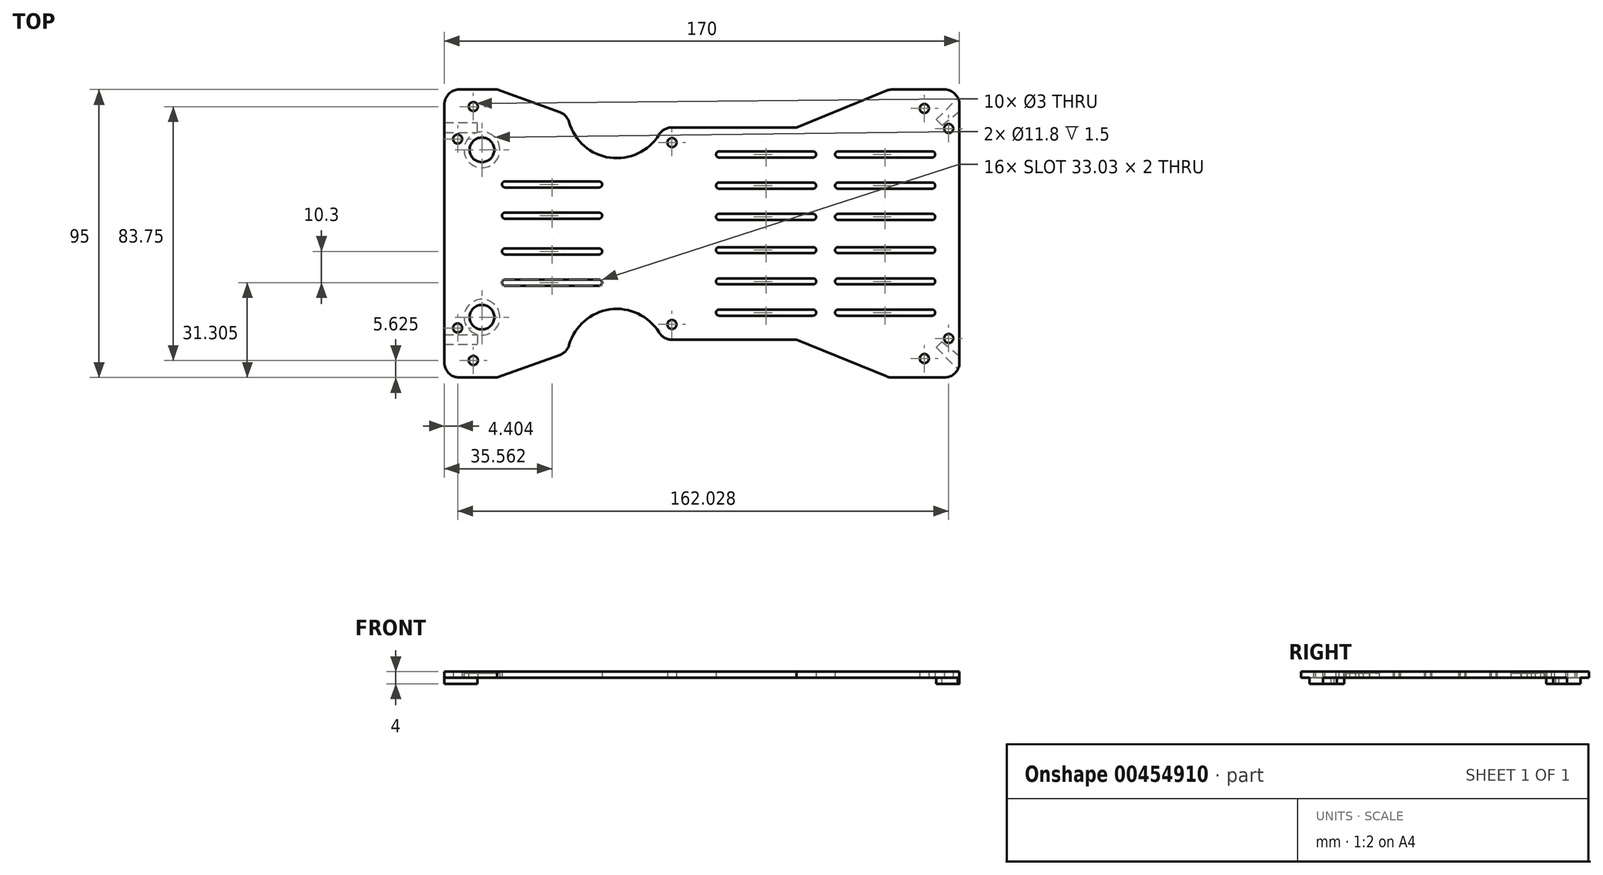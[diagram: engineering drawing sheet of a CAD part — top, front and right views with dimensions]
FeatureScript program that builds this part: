
annotation { "Feature Type Name" : "Feature", "Feature Type Description" : "" }
export const myFeature = defineFeature(function(context is Context, id is Id, definition is map)
    precondition{}
    {
        {
            var Q0;
            Q0=qCreatedBy(makeId("Top.planeOp"),FACE);
            var sketch = newSketch(context, id + "F0", { "sketchPlane" : qUnion([Q0])});
            skLineSegment(sketch, "E0.top", {"start": v(-5, 47.5) * mm, "end": v(-22.22, 47.5) * mm});
            skLineSegment(sketch, "E0.left", {"start": v(0, 35) * mm, "end": v(0, 42.5) * mm});
            skPoint(sketch, "E1.startSnap0", {"position": v(-23.2, 41.25) * mm});
            skPoint(sketch, "E1.startSnap1", {"position": v(-11.6, 47.5) * mm});
            skArc(sketch, "E2", {"start": v(-128.81, 36.72) * mm, "mid": v(-115.3, 25.02) * mm, "end": v(-99.14, 32.63) * mm});
            skLineSegment(sketch, "E3.trimOffspring", {"start": v(-94.88, 35) * mm, "end": v(-53.78, 35) * mm});
            skPoint(sketch, "E1.start.orphan", {"position": v(-11.6, 41.25) * mm});
            skCircle(sketch, "E4", {"center": v(-113.07, 41.25) * mm, "radius": 12.55 * mm, "construction": true});
            skLineSegment(sketch, "E5.top", {"start": v(-165, 47.5) * mm, "end": v(-149.65, 47.5) * mm});
            skLineSegment(sketch, "E5.left", {"start": v(-170, 35) * mm, "end": v(-170, 42.5) * mm});
            skLineSegment(sketch, "E6", {"start": v(-160.43, 41.87) * mm, "end": v(-136.46, 59) * mm, "construction": true});
            skPoint(sketch, "E6.startSnap0", {"position": v(-149.65, 47.5) * mm});
            skPoint(sketch, "E6.startSnap1", {"position": v(-170, 41.25) * mm});
            skLineSegment(sketch, "E7", {"start": v(-136.46, 59) * mm, "end": v(-62.44, 61.85) * mm, "construction": true});
            skLineSegment(sketch, "E8", {"start": v(-160.43, 41.87) * mm, "end": v(-62.44, 61.85) * mm, "construction": true});
            skCircle(sketch, "E9", {"center": v(-62.44, 61.85) * mm, "radius": 12.62 * mm, "construction": true});
            skLineSegment(sketch, "E10", {"start": v(-24.11, 47.13) * mm, "end": v(-53.78, 35) * mm});
            skCircle(sketch, "E11", {"center": v(-157.56, 27.6) * mm, "radius": 4.06 * mm});
            skPoint(sketch, "E0.bottom.end.orphan", {"position": v(-23.2, 35) * mm});
            skPoint(sketch, "E12.middle", {"position": v(-37.46, 31.5) * mm});
            skLineSegment(sketch, "E13", {"start": v(-131.92, 40.04) * mm, "end": v(-152.56, 47.5) * mm});
            skPoint(sketch, "E5.right.end.orphan", {"position": v(-129.3, 47.5) * mm});
            skPoint(sketch, "E14.visualSharp", {"position": v(-170, 47.5) * mm});
            skArc(sketch, "E14.filletArc", {"start": v(-165, 47.5) * mm, "mid": v(-168.54, 46.04) * mm, "end": v(-170, 42.5) * mm});
            skLineSegment(sketch, "E15", {"start": v(-2.46, 0) * mm, "end": v(-170, 0) * mm, "construction": true});
            skLineSegment(sketch, "E16", {"start": v(0, 35) * mm, "end": v(0, 0) * mm});
            skLineSegment(sketch, "E17", {"start": v(-170, 35) * mm, "end": v(-170, 0) * mm});
            skPoint(sketch, "E18.visualSharp", {"position": v(-129.3, 39.1) * mm});
            skArc(sketch, "E18.filletArc", {"start": v(-128.81, 36.72) * mm, "mid": v(-129.96, 38.75) * mm, "end": v(-131.92, 40.04) * mm});
            skPoint(sketch, "E19.visualSharp", {"position": v(-23.2, 47.5) * mm});
            skArc(sketch, "E19.filletArc", {"start": v(-22.22, 47.5) * mm, "mid": v(-23.19, 47.4) * mm, "end": v(-24.11, 47.13) * mm});
            skPoint(sketch, "E20.visualSharp", {"position": v(0, 47.5) * mm});
            skArc(sketch, "E20.filletArc", {"start": v(0, 42.5) * mm, "mid": v(-1.46, 46.04) * mm, "end": v(-5, 47.5) * mm});
            skPoint(sketch, "E21.visualSharp", {"position": v(-97.92, 35) * mm});
            skArc(sketch, "E21.filletArc", {"start": v(-94.88, 35) * mm, "mid": v(-97.32, 34.37) * mm, "end": v(-99.14, 32.63) * mm});
            skCircle(sketch, "E22", {"center": v(-94.88, 30) * mm, "radius": 1.5 * mm});
            skCircle(sketch, "E23", {"center": v(-165.6, 31.16) * mm, "radius": 1.5 * mm});
            skCircle(sketch, "E24", {"center": v(-3.57, 34.62) * mm, "radius": 1.5 * mm});
            skCircle(sketch, "E25", {"center": v(-11.6, 41.25) * mm, "radius": 1.5 * mm});
            skCircle(sketch, "E26", {"center": v(-160.43, 41.87) * mm, "radius": 1.5 * mm});
            skLineSegment(sketch, "E27", {"start": v(-9, 26.08) * mm, "end": v(-40.04, 26.08) * mm, "construction": true});
            skArc(sketch, "E28.0.startCap", {"start": v(-9, 27.08) * mm, "mid": v(-8, 26.08) * mm, "end": v(-9, 25.08) * mm});
            skArc(sketch, "E28.0.endCap", {"start": v(-40.04, 25.08) * mm, "mid": v(-41.04, 26.08) * mm, "end": v(-40.04, 27.08) * mm});
            skLineSegment(sketch, "E28.0.left", {"start": v(-9, 25.08) * mm, "end": v(-40.04, 25.08) * mm});
            skLineSegment(sketch, "E28.0.right", {"start": v(-9, 27.08) * mm, "end": v(-40.04, 27.08) * mm});
            skLineSegment(sketch, "E29.0.1.0", {"start": v(-9, 16.78) * mm, "end": v(-40.04, 16.78) * mm});
            skLineSegment(sketch, "E29.0.1.1", {"start": v(-9, 14.78) * mm, "end": v(-40.04, 14.78) * mm});
            skLineSegment(sketch, "E29.0.1.2", {"start": v(-9, 15.78) * mm, "end": v(-40.04, 15.78) * mm, "construction": true});
            skArc(sketch, "E29.0.1.3", {"start": v(-9, 16.78) * mm, "mid": v(-8, 15.78) * mm, "end": v(-9, 14.78) * mm});
            skArc(sketch, "E29.0.1.4", {"start": v(-40.04, 14.78) * mm, "mid": v(-41.04, 15.78) * mm, "end": v(-40.04, 16.78) * mm});
            skLineSegment(sketch, "E29.0.2.0", {"start": v(-9, 6.48) * mm, "end": v(-40.04, 6.48) * mm});
            skLineSegment(sketch, "E29.0.2.1", {"start": v(-9, 4.48) * mm, "end": v(-40.04, 4.48) * mm});
            skLineSegment(sketch, "E29.0.2.2", {"start": v(-9, 5.48) * mm, "end": v(-40.04, 5.48) * mm, "construction": true});
            skArc(sketch, "E29.0.2.3", {"start": v(-9, 6.48) * mm, "mid": v(-8, 5.48) * mm, "end": v(-9, 4.48) * mm});
            skArc(sketch, "E29.0.2.4", {"start": v(-40.04, 4.48) * mm, "mid": v(-41.04, 5.48) * mm, "end": v(-40.04, 6.48) * mm});
            skLineSegment(sketch, "E29.1.0.0", {"start": v(-48.3, 27.08) * mm, "end": v(-79.34, 27.08) * mm});
            skLineSegment(sketch, "E29.1.0.1", {"start": v(-48.3, 25.08) * mm, "end": v(-79.34, 25.08) * mm});
            skLineSegment(sketch, "E29.1.0.2", {"start": v(-48.3, 26.08) * mm, "end": v(-79.34, 26.08) * mm, "construction": true});
            skArc(sketch, "E29.1.0.3", {"start": v(-48.3, 27.08) * mm, "mid": v(-47.3, 26.08) * mm, "end": v(-48.3, 25.08) * mm});
            skArc(sketch, "E29.1.0.4", {"start": v(-79.34, 25.08) * mm, "mid": v(-80.34, 26.08) * mm, "end": v(-79.34, 27.08) * mm});
            skLineSegment(sketch, "E29.1.1.0", {"start": v(-48.3, 16.78) * mm, "end": v(-79.34, 16.78) * mm});
            skLineSegment(sketch, "E29.1.1.1", {"start": v(-48.3, 14.78) * mm, "end": v(-79.34, 14.78) * mm});
            skLineSegment(sketch, "E29.1.1.2", {"start": v(-48.3, 15.78) * mm, "end": v(-79.34, 15.78) * mm, "construction": true});
            skArc(sketch, "E29.1.1.3", {"start": v(-48.3, 16.78) * mm, "mid": v(-47.3, 15.78) * mm, "end": v(-48.3, 14.78) * mm});
            skArc(sketch, "E29.1.1.4", {"start": v(-79.34, 14.78) * mm, "mid": v(-80.34, 15.78) * mm, "end": v(-79.34, 16.78) * mm});
            skLineSegment(sketch, "E29.1.2.0", {"start": v(-48.3, 6.48) * mm, "end": v(-79.34, 6.48) * mm});
            skLineSegment(sketch, "E29.1.2.1", {"start": v(-48.3, 4.48) * mm, "end": v(-79.34, 4.48) * mm});
            skLineSegment(sketch, "E29.1.2.2", {"start": v(-48.3, 5.48) * mm, "end": v(-79.34, 5.48) * mm, "construction": true});
            skArc(sketch, "E29.1.2.3", {"start": v(-48.3, 6.48) * mm, "mid": v(-47.3, 5.48) * mm, "end": v(-48.3, 4.48) * mm});
            skArc(sketch, "E29.1.2.4", {"start": v(-79.34, 4.48) * mm, "mid": v(-80.34, 5.48) * mm, "end": v(-79.34, 6.48) * mm});
            skLineSegment(sketch, "E29.direction1", {"start": v(-40.04, 25.08) * mm, "end": v(-79.34, 25.08) * mm, "construction": true});
            skLineSegment(sketch, "E29.direction2", {"start": v(-40.04, 25.08) * mm, "end": v(-40.04, 14.78) * mm, "construction": true});
            skLineSegment(sketch, "E30.1.1.0", {"start": v(-118.92, 17.2) * mm, "end": v(-149.95, 17.2) * mm});
            skLineSegment(sketch, "E30.1.1.1", {"start": v(-118.92, 15.2) * mm, "end": v(-149.95, 15.2) * mm});
            skLineSegment(sketch, "E30.1.1.2", {"start": v(-118.92, 16.2) * mm, "end": v(-149.95, 16.2) * mm, "construction": true});
            skArc(sketch, "E30.1.1.3", {"start": v(-118.92, 17.2) * mm, "mid": v(-117.92, 16.2) * mm, "end": v(-118.92, 15.2) * mm});
            skArc(sketch, "E30.1.1.4", {"start": v(-149.95, 15.2) * mm, "mid": v(-150.95, 16.2) * mm, "end": v(-149.95, 17.2) * mm});
            skLineSegment(sketch, "E30.1.2.0", {"start": v(-118.92, 6.9) * mm, "end": v(-149.95, 6.9) * mm});
            skLineSegment(sketch, "E30.1.2.1", {"start": v(-118.92, 4.9) * mm, "end": v(-149.95, 4.9) * mm});
            skLineSegment(sketch, "E30.1.2.2", {"start": v(-118.92, 5.9) * mm, "end": v(-149.95, 5.9) * mm, "construction": true});
            skArc(sketch, "E30.1.2.3", {"start": v(-118.92, 6.9) * mm, "mid": v(-117.92, 5.9) * mm, "end": v(-118.92, 4.9) * mm});
            skArc(sketch, "E30.1.2.4", {"start": v(-149.95, 4.9) * mm, "mid": v(-150.95, 5.9) * mm, "end": v(-149.95, 6.9) * mm});
            skLineSegment(sketch, "E31.MirrorCS", {"start": v(-40.04, -25.08) * mm, "end": v(-40.04, -14.78) * mm, "construction": true});
            skLineSegment(sketch, "E32.MirrorCS", {"start": v(-170, -35) * mm, "end": v(-170, -42.5) * mm});
            skLineSegment(sketch, "E33.MirrorCS", {"start": v(0, -35) * mm, "end": v(0, -42.5) * mm});
            skLineSegment(sketch, "E34.MirrorCS", {"start": v(-48.3, -6.48) * mm, "end": v(-79.34, -6.48) * mm});
            skLineSegment(sketch, "E35.MirrorCS", {"start": v(-9, -6.48) * mm, "end": v(-40.04, -6.48) * mm});
            skLineSegment(sketch, "E36.MirrorCS", {"start": v(-118.92, -15.2) * mm, "end": v(-149.95, -15.2) * mm});
            skLineSegment(sketch, "E37.MirrorCS", {"start": v(-5, -47.5) * mm, "end": v(-22.22, -47.5) * mm});
            skLineSegment(sketch, "E38.MirrorCS", {"start": v(-9, -14.78) * mm, "end": v(-40.04, -14.78) * mm});
            skLineSegment(sketch, "E39.MirrorCS", {"start": v(-48.3, -14.78) * mm, "end": v(-79.34, -14.78) * mm});
            skCircle(sketch, "E40.MirrorC", {"center": v(-157.56, -27.6) * mm, "radius": 4.06 * mm});
            skLineSegment(sketch, "E41.MirrorCS", {"start": v(-118.92, -6.9) * mm, "end": v(-149.95, -6.9) * mm});
            skLineSegment(sketch, "E42.MirrorCS", {"start": v(-165, -47.5) * mm, "end": v(-149.65, -47.5) * mm});
            skPoint(sketch, "E43.MirrorP", {"position": v(-37.46, -31.5) * mm});
            skLineSegment(sketch, "E44.MirrorCS", {"start": v(-118.92, -5.9) * mm, "end": v(-149.95, -5.9) * mm, "construction": true});
            skPoint(sketch, "E45.MirrorP", {"position": v(-129.3, -47.5) * mm});
            skLineSegment(sketch, "E46.MirrorCS", {"start": v(-9, -15.78) * mm, "end": v(-40.04, -15.78) * mm, "construction": true});
            skPoint(sketch, "E47.MirrorP", {"position": v(-23.2, -35) * mm});
            skLineSegment(sketch, "E48.MirrorCS", {"start": v(-48.3, -4.48) * mm, "end": v(-79.34, -4.48) * mm});
            skPoint(sketch, "E49.MirrorP", {"position": v(-170, -47.5) * mm});
            skLineSegment(sketch, "E50.MirrorCS", {"start": v(-48.3, -5.48) * mm, "end": v(-79.34, -5.48) * mm, "construction": true});
            skLineSegment(sketch, "E51.MirrorCS", {"start": v(-9, -4.48) * mm, "end": v(-40.04, -4.48) * mm});
            skLineSegment(sketch, "E52.MirrorCS", {"start": v(-9, -5.48) * mm, "end": v(-40.04, -5.48) * mm, "construction": true});
            skPoint(sketch, "E53.MirrorP", {"position": v(-129.3, -39.1) * mm});
            skLineSegment(sketch, "E54.MirrorCS", {"start": v(-40.04, -25.08) * mm, "end": v(-79.34, -25.08) * mm, "construction": true});
            skPoint(sketch, "E55.MirrorP", {"position": v(-23.2, -41.25) * mm});
            skPoint(sketch, "E56.MirrorP", {"position": v(-11.6, -41.25) * mm});
            skPoint(sketch, "E57.MirrorP", {"position": v(0, -47.5) * mm});
            skLineSegment(sketch, "E58.MirrorCS", {"start": v(-48.3, -27.08) * mm, "end": v(-79.34, -27.08) * mm});
            skPoint(sketch, "E59.MirrorP", {"position": v(-23.2, -47.5) * mm});
            skLineSegment(sketch, "E60.MirrorCS", {"start": v(-160.43, -41.87) * mm, "end": v(-62.44, -61.85) * mm, "construction": true});
            skCircle(sketch, "E61.MirrorC", {"center": v(-113.07, -41.25) * mm, "radius": 12.55 * mm, "construction": true});
            skLineSegment(sketch, "E62.MirrorCS", {"start": v(-24.11, -47.13) * mm, "end": v(-53.78, -35) * mm});
            skLineSegment(sketch, "E63.MirrorCS", {"start": v(-94.88, -35) * mm, "end": v(-53.78, -35) * mm});
            skLineSegment(sketch, "E64.MirrorCS", {"start": v(-9, -25.08) * mm, "end": v(-40.04, -25.08) * mm});
            skLineSegment(sketch, "E65.MirrorCS", {"start": v(-160.43, -41.87) * mm, "end": v(-136.46, -59) * mm, "construction": true});
            skLineSegment(sketch, "E66.MirrorCS", {"start": v(-9, -16.78) * mm, "end": v(-40.04, -16.78) * mm});
            skLineSegment(sketch, "E67.MirrorCS", {"start": v(-48.3, -26.08) * mm, "end": v(-79.34, -26.08) * mm, "construction": true});
            skLineSegment(sketch, "E68.MirrorCS", {"start": v(-136.46, -59) * mm, "end": v(-62.44, -61.85) * mm, "construction": true});
            skPoint(sketch, "E69.MirrorP", {"position": v(-170, -41.25) * mm});
            skLineSegment(sketch, "E70.MirrorCS", {"start": v(-9, -26.08) * mm, "end": v(-40.04, -26.08) * mm, "construction": true});
            skLineSegment(sketch, "E71.MirrorCS", {"start": v(-118.92, -17.2) * mm, "end": v(-149.95, -17.2) * mm});
            skLineSegment(sketch, "E72.MirrorCS", {"start": v(0, -35) * mm, "end": v(0, 0) * mm});
            skPoint(sketch, "E73.MirrorP", {"position": v(-97.92, -35) * mm});
            skCircle(sketch, "E74.MirrorC", {"center": v(-62.44, -61.85) * mm, "radius": 12.62 * mm, "construction": true});
            skPoint(sketch, "E75.MirrorP", {"position": v(-11.6, -47.5) * mm});
            skArc(sketch, "E76.MirrorCS", {"start": v(-128.81, -36.72) * mm, "mid": v(-115.3, -25.02) * mm, "end": v(-99.14, -32.63) * mm});
            skLineSegment(sketch, "E77.MirrorCS", {"start": v(-9, -27.08) * mm, "end": v(-40.04, -27.08) * mm});
            skLineSegment(sketch, "E78.MirrorCS", {"start": v(-48.3, -16.78) * mm, "end": v(-79.34, -16.78) * mm});
            skLineSegment(sketch, "E79.MirrorCS", {"start": v(-118.92, -16.2) * mm, "end": v(-149.95, -16.2) * mm, "construction": true});
            skLineSegment(sketch, "E80.MirrorCS", {"start": v(-48.3, -15.78) * mm, "end": v(-79.34, -15.78) * mm, "construction": true});
            skLineSegment(sketch, "E81.MirrorCS", {"start": v(-118.92, -4.9) * mm, "end": v(-149.95, -4.9) * mm});
            skPoint(sketch, "E82.MirrorP", {"position": v(-149.65, -47.5) * mm});
            skLineSegment(sketch, "E83.MirrorCS", {"start": v(-170, -35) * mm, "end": v(-170, 0) * mm});
            skLineSegment(sketch, "E84.MirrorCS", {"start": v(-131.92, -40.04) * mm, "end": v(-152.56, -47.5) * mm});
            skArc(sketch, "E85.MirrorCS", {"start": v(-118.92, -6.9) * mm, "mid": v(-117.92, -5.9) * mm, "end": v(-118.92, -4.9) * mm});
            skArc(sketch, "E86.MirrorCS", {"start": v(-9, -27.08) * mm, "mid": v(-8, -26.08) * mm, "end": v(-9, -25.08) * mm});
            skArc(sketch, "E87.MirrorCS", {"start": v(-40.04, -25.08) * mm, "mid": v(-41.04, -26.08) * mm, "end": v(-40.04, -27.08) * mm});
            skArc(sketch, "E88.MirrorCS", {"start": v(-149.95, -4.9) * mm, "mid": v(-150.95, -5.9) * mm, "end": v(-149.95, -6.9) * mm});
            skArc(sketch, "E89.MirrorCS", {"start": v(-40.04, -14.78) * mm, "mid": v(-41.04, -15.78) * mm, "end": v(-40.04, -16.78) * mm});
            skCircle(sketch, "E90.MirrorC", {"center": v(-94.88, -30) * mm, "radius": 1.5 * mm});
            skArc(sketch, "E91.MirrorCS", {"start": v(-9, -6.48) * mm, "mid": v(-8, -5.48) * mm, "end": v(-9, -4.48) * mm});
            skArc(sketch, "E92.MirrorCS", {"start": v(-22.22, -47.5) * mm, "mid": v(-23.19, -47.4) * mm, "end": v(-24.11, -47.13) * mm});
            skArc(sketch, "E93.MirrorCS", {"start": v(-79.34, -14.78) * mm, "mid": v(-80.34, -15.78) * mm, "end": v(-79.34, -16.78) * mm});
            skArc(sketch, "E94.MirrorCS", {"start": v(-9, -16.78) * mm, "mid": v(-8, -15.78) * mm, "end": v(-9, -14.78) * mm});
            skCircle(sketch, "E95.MirrorC", {"center": v(-160.43, -41.87) * mm, "radius": 1.5 * mm});
            skArc(sketch, "E96.MirrorCS", {"start": v(-149.95, -15.2) * mm, "mid": v(-150.95, -16.2) * mm, "end": v(-149.95, -17.2) * mm});
            skArc(sketch, "E97.MirrorCS", {"start": v(-128.81, -36.72) * mm, "mid": v(-129.96, -38.75) * mm, "end": v(-131.92, -40.04) * mm});
            skArc(sketch, "E98.MirrorCS", {"start": v(-48.3, -16.78) * mm, "mid": v(-47.3, -15.78) * mm, "end": v(-48.3, -14.78) * mm});
            skArc(sketch, "E99.MirrorCS", {"start": v(-94.88, -35) * mm, "mid": v(-97.32, -34.37) * mm, "end": v(-99.14, -32.63) * mm});
            skArc(sketch, "E100.MirrorCS", {"start": v(-48.3, -6.48) * mm, "mid": v(-47.3, -5.48) * mm, "end": v(-48.3, -4.48) * mm});
            skArc(sketch, "E101.MirrorCS", {"start": v(-79.34, -4.48) * mm, "mid": v(-80.34, -5.48) * mm, "end": v(-79.34, -6.48) * mm});
            skArc(sketch, "E102.MirrorCS", {"start": v(-40.04, -4.48) * mm, "mid": v(-41.04, -5.48) * mm, "end": v(-40.04, -6.48) * mm});
            skCircle(sketch, "E103.MirrorC", {"center": v(-11.6, -41.25) * mm, "radius": 1.5 * mm});
            skArc(sketch, "E104.MirrorCS", {"start": v(-79.34, -25.08) * mm, "mid": v(-80.34, -26.08) * mm, "end": v(-79.34, -27.08) * mm});
            skArc(sketch, "E105.MirrorCS", {"start": v(-48.3, -27.08) * mm, "mid": v(-47.3, -26.08) * mm, "end": v(-48.3, -25.08) * mm});
            skArc(sketch, "E106.MirrorCS", {"start": v(-118.92, -17.2) * mm, "mid": v(-117.92, -16.2) * mm, "end": v(-118.92, -15.2) * mm});
            skArc(sketch, "E107.MirrorCS", {"start": v(0, -42.5) * mm, "mid": v(-1.46, -46.04) * mm, "end": v(-5, -47.5) * mm});
            skCircle(sketch, "E108.MirrorC", {"center": v(-165.6, -31.16) * mm, "radius": 1.5 * mm});
            skCircle(sketch, "E109.MirrorC", {"center": v(-3.57, -34.62) * mm, "radius": 1.5 * mm});
            skLineSegment(sketch, "E110.MirrorCS", {"start": v(-48.3, -25.08) * mm, "end": v(-79.34, -25.08) * mm});
            skArc(sketch, "E111.MirrorCS", {"start": v(-165, -47.5) * mm, "mid": v(-168.54, -46.04) * mm, "end": v(-170, -42.5) * mm});
            skSolve(sketch);
        }
        {
            var Q0;
            Q0=qSketchRegion(id+"F0",true);
            extrude(context, id + "F1", {"entities" : qUnion([Q0]), "depth" : 2 * mm});
        }
        {
            var Q0;
            Q0=makeQuery(id+"F1.opExtrude","CAP_FACE",FACE,{"disambiguationData":[OSD([sQuery(id+"F0.wireOp",EDGE,"E0.top"),sQuery(id+"F0.wireOp",EDGE,"E0.left"),sQuery(id+"F0.wireOp",EDGE,"E2"),sQuery(id+"F0.wireOp",EDGE,"E3.trimOffspring"),sQuery(id+"F0.wireOp",EDGE,"E5.top"),sQuery(id+"F0.wireOp",EDGE,"E5.left"),sQuery(id+"F0.wireOp",EDGE,"7hJqdO40-9QEB-ep9W-JTcp-znnLO8iOH2ny"),sQuery(id+"F0.wireOp",EDGE,"yaqOU6vn-vtul-Jn4A-1Bdt-kECmfQPkav5v"),sQuery(id+"F0.wireOp",EDGE,"r8IJrCJv-crzM-KIvY-DkAr-MW3v6tCYtiw1"),sQuery(id+"F0.wireOp",EDGE,"jzMd41p7-Ak69-SiEM-pOr1-xVNg9LxxrAfh"),sQuery(id+"F0.wireOp",EDGE,"fxCpGdvF-k1nJ-6rw2-18lv-cCig44xFyPOT"),sQuery(id+"F0.wireOp",EDGE,"3vhJkwcW-7L6n-dbvg-KpTP-31G8Jv8qNSP8"),sQuery(id+"F0.wireOp",EDGE,"9XNVBvv0-zH1r-9cPB-NFeU-YQdWjPXlst3P"),sQuery(id+"F0.wireOp",EDGE,"y3D83JcK-dgKw-NrD8-Es56-h46w4wRxeLdj"),sQuery(id+"F0.wireOp",EDGE,"E10"),sQuery(id+"F0.wireOp",EDGE,"E11"),sQuery(id+"F0.wireOp",EDGE,"axs33Ezf-adaq-kjD9-MvXq-XhUTkXVeFDVn"),sQuery(id+"F0.wireOp",EDGE,"E12.bottom"),sQuery(id+"F0.wireOp",EDGE,"E12.top"),sQuery(id+"F0.wireOp",EDGE,"E12.left"),sQuery(id+"F0.wireOp",EDGE,"E12.right"),sQuery(id+"F0.wireOp",EDGE,"E13"),sQuery(id+"F0.wireOp",EDGE,"E14.filletArc"),sQuery(id+"F0.wireOp",EDGE,"E16"),sQuery(id+"F0.wireOp",EDGE,"E17"),sQuery(id+"F0.wireOp",EDGE,"E18.filletArc"),sQuery(id+"F0.wireOp",EDGE,"E19.filletArc"),sQuery(id+"F0.wireOp",EDGE,"E20.filletArc"),sQuery(id+"F0.wireOp",EDGE,"E21.filletArc"),sQuery(id+"F0.wireOp",EDGE,"E22"),sQuery(id+"F0.wireOp",EDGE,"E23"),sQuery(id+"F0.wireOp",EDGE,"E24"),sQuery(id+"F0.wireOp",EDGE,"dc92d004-a6ad-41b4-b321-0510745f16cf0.MirrorC"),sQuery(id+"F0.wireOp",EDGE,"dc92d004-a6ad-41b4-b321-0510745f16cf1.MirrorCS"),sQuery(id+"F0.wireOp",EDGE,"dc92d004-a6ad-41b4-b321-0510745f16cf2.MirrorC"),sQuery(id+"F0.wireOp",EDGE,"dc92d004-a6ad-41b4-b321-0510745f16cf3.MirrorCS"),sQuery(id+"F0.wireOp",EDGE,"dc92d004-a6ad-41b4-b321-0510745f16cf4.MirrorCS"),sQuery(id+"F0.wireOp",EDGE,"dc92d004-a6ad-41b4-b321-0510745f16cf5.MirrorCS"),sQuery(id+"F0.wireOp",EDGE,"dc92d004-a6ad-41b4-b321-0510745f16cf6.MirrorCS"),sQuery(id+"F0.wireOp",EDGE,"dc92d004-a6ad-41b4-b321-0510745f16cf7.MirrorCS"),sQuery(id+"F0.wireOp",EDGE,"dc92d004-a6ad-41b4-b321-0510745f16cf8.MirrorCS"),sQuery(id+"F0.wireOp",EDGE,"dc92d004-a6ad-41b4-b321-0510745f16cf9.MirrorCS"),sQuery(id+"F0.wireOp",EDGE,"dc92d004-a6ad-41b4-b321-0510745f16cf10.MirrorCS"),sQuery(id+"F0.wireOp",EDGE,"dc92d004-a6ad-41b4-b321-0510745f16cf11.MirrorCS"),sQuery(id+"F0.wireOp",EDGE,"dc92d004-a6ad-41b4-b321-0510745f16cf12.MirrorC"),sQuery(id+"F0.wireOp",EDGE,"dc92d004-a6ad-41b4-b321-0510745f16cf13.MirrorCS"),sQuery(id+"F0.wireOp",EDGE,"dc92d004-a6ad-41b4-b321-0510745f16cf14.MirrorC"),sQuery(id+"F0.wireOp",EDGE,"dc92d004-a6ad-41b4-b321-0510745f16cf15.MirrorCS"),sQuery(id+"F0.wireOp",EDGE,"dc92d004-a6ad-41b4-b321-0510745f16cf17.MirrorCS"),sQuery(id+"F0.wireOp",EDGE,"dc92d004-a6ad-41b4-b321-0510745f16cf18.MirrorCS"),sQuery(id+"F0.wireOp",EDGE,"dc92d004-a6ad-41b4-b321-0510745f16cf19.MirrorC"),sQuery(id+"F0.wireOp",EDGE,"dc92d004-a6ad-41b4-b321-0510745f16cf20.MirrorCS"),sQuery(id+"F0.wireOp",EDGE,"dc92d004-a6ad-41b4-b321-0510745f16cf26.MirrorCS"),sQuery(id+"F0.wireOp",EDGE,"dc92d004-a6ad-41b4-b321-0510745f16cf27.MirrorCS"),sQuery(id+"F0.wireOp",EDGE,"dc92d004-a6ad-41b4-b321-0510745f16cf28.MirrorCS"),sQuery(id+"F0.wireOp",EDGE,"dc92d004-a6ad-41b4-b321-0510745f16cf31.MirrorCS"),sQuery(id+"F0.wireOp",EDGE,"dc92d004-a6ad-41b4-b321-0510745f16cf32.MirrorCS"),sQuery(id+"F0.wireOp",EDGE,"dc92d004-a6ad-41b4-b321-0510745f16cf38.MirrorCS"),sQuery(id+"F0.wireOp",EDGE,"dc92d004-a6ad-41b4-b321-0510745f16cf42.MirrorCS"),sQuery(id+"F0.wireOp",EDGE,"dc92d004-a6ad-41b4-b321-0510745f16cf46.MirrorCS"),sQuery(id+"F0.wireOp",EDGE,"dc92d004-a6ad-41b4-b321-0510745f16cf49.MirrorCS"),sQuery(id+"F0.wireOp",EDGE,"dc92d004-a6ad-41b4-b321-0510745f16cf52.MirrorC"),sQuery(id+"F0.wireOp",EDGE,"dc92d004-a6ad-41b4-b321-0510745f16cf53.MirrorCS"),sQuery(id+"F0.wireOp",EDGE,"dc92d004-a6ad-41b4-b321-0510745f16cf54.MirrorCS"),sQuery(id+"F0.wireOp",EDGE,"dc92d004-a6ad-41b4-b321-0510745f16cf55.MirrorCS"),sQuery(id+"F0.wireOp",EDGE,"E25"),sQuery(id+"F0.wireOp",EDGE,"E26"),sQuery(id+"F0.wireOp",EDGE,"ffa57ce4-e106-4af1-8c53-b98dc5f750d70.MirrorC"),sQuery(id+"F0.wireOp",EDGE,"3e98f3d7-1223-4975-97da-47207ce6f79a0.MirrorC")])],"isStart":true});
            var sketch = newSketch(context, id + "F2", { "sketchPlane" : qUnion([Q0])});
            skLineSegment(sketch, "E112.bottom", {"start": v(-170, 33.34) * mm, "end": v(-159, 33.34) * mm});
            skLineSegment(sketch, "E112.top", {"start": v(-170, 36.59) * mm, "end": v(-159, 36.59) * mm});
            skLineSegment(sketch, "E112.left", {"start": v(-170, 33.34) * mm, "end": v(-170, 36.59) * mm});
            skLineSegment(sketch, "E112.right", {"start": v(-159, 33.34) * mm, "end": v(-159, 36.59) * mm});
            skLineSegment(sketch, "E113", {"start": v(-160.43, 41.87) * mm, "end": v(-160.43, 36.87) * mm, "construction": true});
            skLineSegment(sketch, "E114", {"start": v(-11.6, 41.25) * mm, "end": v(-8.07, 37.71) * mm, "construction": true});
            skLineSegment(sketch, "E115", {"start": v(-11.6, 41.25) * mm, "end": v(0, 41.25) * mm, "construction": true});
            skLineSegment(sketch, "E116", {"start": v(-7.7, 37.6) * mm, "end": v(-0.54, 44.75) * mm});
            skLineSegment(sketch, "E117", {"start": v(-7.7, 37.6) * mm, "end": v(-5.77, 35.67) * mm});
            skLineSegment(sketch, "E118", {"start": v(-5.77, 35.67) * mm, "end": v(0, 40.31) * mm});
            skArc(sketch, "E119.0", {"start": v(0, 42.5) * mm, "mid": v(-0.14, 43.66) * mm, "end": v(-0.54, 44.75) * mm});
            skLineSegment(sketch, "E120.0", {"start": v(0, 40.31) * mm, "end": v(0, 42.5) * mm});
            skPoint(sketch, "E121.orphan", {"position": v(-5, 47.5) * mm});
            skPoint(sketch, "E122.orphan", {"position": v(0, -42.5) * mm});
            skLineSegment(sketch, "E123", {"start": v(-170, 0) * mm, "end": v(0, 0) * mm, "construction": true});
            skLineSegment(sketch, "E124.MirrorCS", {"start": v(0, -40.31) * mm, "end": v(0, -42.5) * mm});
            skArc(sketch, "E125.MirrorCS", {"start": v(0, -42.5) * mm, "mid": v(-0.14, -43.66) * mm, "end": v(-0.54, -44.75) * mm});
            skLineSegment(sketch, "E126.MirrorCS", {"start": v(-7.7, -37.6) * mm, "end": v(-5.77, -35.67) * mm});
            skLineSegment(sketch, "E127.MirrorCS", {"start": v(-170, -33.34) * mm, "end": v(-170, -36.59) * mm});
            skLineSegment(sketch, "E128.MirrorCS", {"start": v(-159, -33.34) * mm, "end": v(-159, -36.59) * mm});
            skLineSegment(sketch, "E129.MirrorCS", {"start": v(-11.6, -41.25) * mm, "end": v(-8.07, -37.71) * mm, "construction": true});
            skLineSegment(sketch, "E130.MirrorCS", {"start": v(-5.77, -35.67) * mm, "end": v(0, -40.31) * mm});
            skLineSegment(sketch, "E131.MirrorCS", {"start": v(-11.6, -41.25) * mm, "end": v(0, -41.25) * mm, "construction": true});
            skLineSegment(sketch, "E132.MirrorCS", {"start": v(-160.43, -41.87) * mm, "end": v(-160.43, -36.87) * mm, "construction": true});
            skLineSegment(sketch, "E133.MirrorCS", {"start": v(-7.7, -37.6) * mm, "end": v(-0.54, -44.75) * mm});
            skPoint(sketch, "E134.MirrorP", {"position": v(-5, -47.5) * mm});
            skLineSegment(sketch, "E135.MirrorCS", {"start": v(-170, -33.34) * mm, "end": v(-159, -33.34) * mm});
            skLineSegment(sketch, "E136.MirrorCS", {"start": v(-170, -36.59) * mm, "end": v(-159, -36.59) * mm});
            skSolve(sketch);
        }
        {
            var Q0;
            Q0=qSketchRegion(id+"F2",true);
            extrude(context, id + "F3", {"entities" : qUnion([Q0]), "operationType" : NewBodyOperationType.ADD, "depth" : 2 * mm});
        }
        {
            var Q0;
            Q0=makeQuery(id+"F1.opExtrude","CAP_FACE",FACE,{"disambiguationData":[OSD([sQuery(id+"F0.wireOp",EDGE,"E0.top"),sQuery(id+"F0.wireOp",EDGE,"E0.left"),sQuery(id+"F0.wireOp",EDGE,"E2"),sQuery(id+"F0.wireOp",EDGE,"E3.trimOffspring"),sQuery(id+"F0.wireOp",EDGE,"E5.top"),sQuery(id+"F0.wireOp",EDGE,"E5.left"),sQuery(id+"F0.wireOp",EDGE,"7hJqdO40-9QEB-ep9W-JTcp-znnLO8iOH2ny"),sQuery(id+"F0.wireOp",EDGE,"yaqOU6vn-vtul-Jn4A-1Bdt-kECmfQPkav5v"),sQuery(id+"F0.wireOp",EDGE,"r8IJrCJv-crzM-KIvY-DkAr-MW3v6tCYtiw1"),sQuery(id+"F0.wireOp",EDGE,"jzMd41p7-Ak69-SiEM-pOr1-xVNg9LxxrAfh"),sQuery(id+"F0.wireOp",EDGE,"fxCpGdvF-k1nJ-6rw2-18lv-cCig44xFyPOT"),sQuery(id+"F0.wireOp",EDGE,"3vhJkwcW-7L6n-dbvg-KpTP-31G8Jv8qNSP8"),sQuery(id+"F0.wireOp",EDGE,"9XNVBvv0-zH1r-9cPB-NFeU-YQdWjPXlst3P"),sQuery(id+"F0.wireOp",EDGE,"y3D83JcK-dgKw-NrD8-Es56-h46w4wRxeLdj"),sQuery(id+"F0.wireOp",EDGE,"E10"),sQuery(id+"F0.wireOp",EDGE,"E11"),sQuery(id+"F0.wireOp",EDGE,"axs33Ezf-adaq-kjD9-MvXq-XhUTkXVeFDVn"),sQuery(id+"F0.wireOp",EDGE,"E12.bottom"),sQuery(id+"F0.wireOp",EDGE,"E12.top"),sQuery(id+"F0.wireOp",EDGE,"E12.left"),sQuery(id+"F0.wireOp",EDGE,"E12.right"),sQuery(id+"F0.wireOp",EDGE,"E13"),sQuery(id+"F0.wireOp",EDGE,"E14.filletArc"),sQuery(id+"F0.wireOp",EDGE,"E16"),sQuery(id+"F0.wireOp",EDGE,"E17"),sQuery(id+"F0.wireOp",EDGE,"E18.filletArc"),sQuery(id+"F0.wireOp",EDGE,"E19.filletArc"),sQuery(id+"F0.wireOp",EDGE,"E20.filletArc"),sQuery(id+"F0.wireOp",EDGE,"E21.filletArc"),sQuery(id+"F0.wireOp",EDGE,"E22"),sQuery(id+"F0.wireOp",EDGE,"E23"),sQuery(id+"F0.wireOp",EDGE,"E24"),sQuery(id+"F0.wireOp",EDGE,"dc92d004-a6ad-41b4-b321-0510745f16cf0.MirrorC"),sQuery(id+"F0.wireOp",EDGE,"dc92d004-a6ad-41b4-b321-0510745f16cf1.MirrorCS"),sQuery(id+"F0.wireOp",EDGE,"dc92d004-a6ad-41b4-b321-0510745f16cf2.MirrorC"),sQuery(id+"F0.wireOp",EDGE,"dc92d004-a6ad-41b4-b321-0510745f16cf3.MirrorCS"),sQuery(id+"F0.wireOp",EDGE,"dc92d004-a6ad-41b4-b321-0510745f16cf4.MirrorCS"),sQuery(id+"F0.wireOp",EDGE,"dc92d004-a6ad-41b4-b321-0510745f16cf5.MirrorCS"),sQuery(id+"F0.wireOp",EDGE,"dc92d004-a6ad-41b4-b321-0510745f16cf6.MirrorCS"),sQuery(id+"F0.wireOp",EDGE,"dc92d004-a6ad-41b4-b321-0510745f16cf7.MirrorCS"),sQuery(id+"F0.wireOp",EDGE,"dc92d004-a6ad-41b4-b321-0510745f16cf8.MirrorCS"),sQuery(id+"F0.wireOp",EDGE,"dc92d004-a6ad-41b4-b321-0510745f16cf9.MirrorCS"),sQuery(id+"F0.wireOp",EDGE,"dc92d004-a6ad-41b4-b321-0510745f16cf10.MirrorCS"),sQuery(id+"F0.wireOp",EDGE,"dc92d004-a6ad-41b4-b321-0510745f16cf11.MirrorCS"),sQuery(id+"F0.wireOp",EDGE,"dc92d004-a6ad-41b4-b321-0510745f16cf12.MirrorC"),sQuery(id+"F0.wireOp",EDGE,"dc92d004-a6ad-41b4-b321-0510745f16cf13.MirrorCS"),sQuery(id+"F0.wireOp",EDGE,"dc92d004-a6ad-41b4-b321-0510745f16cf14.MirrorC"),sQuery(id+"F0.wireOp",EDGE,"dc92d004-a6ad-41b4-b321-0510745f16cf15.MirrorCS"),sQuery(id+"F0.wireOp",EDGE,"dc92d004-a6ad-41b4-b321-0510745f16cf17.MirrorCS"),sQuery(id+"F0.wireOp",EDGE,"dc92d004-a6ad-41b4-b321-0510745f16cf18.MirrorCS"),sQuery(id+"F0.wireOp",EDGE,"dc92d004-a6ad-41b4-b321-0510745f16cf19.MirrorC"),sQuery(id+"F0.wireOp",EDGE,"dc92d004-a6ad-41b4-b321-0510745f16cf20.MirrorCS"),sQuery(id+"F0.wireOp",EDGE,"dc92d004-a6ad-41b4-b321-0510745f16cf26.MirrorCS"),sQuery(id+"F0.wireOp",EDGE,"dc92d004-a6ad-41b4-b321-0510745f16cf27.MirrorCS"),sQuery(id+"F0.wireOp",EDGE,"dc92d004-a6ad-41b4-b321-0510745f16cf28.MirrorCS"),sQuery(id+"F0.wireOp",EDGE,"dc92d004-a6ad-41b4-b321-0510745f16cf31.MirrorCS"),sQuery(id+"F0.wireOp",EDGE,"dc92d004-a6ad-41b4-b321-0510745f16cf32.MirrorCS"),sQuery(id+"F0.wireOp",EDGE,"dc92d004-a6ad-41b4-b321-0510745f16cf38.MirrorCS"),sQuery(id+"F0.wireOp",EDGE,"dc92d004-a6ad-41b4-b321-0510745f16cf42.MirrorCS"),sQuery(id+"F0.wireOp",EDGE,"dc92d004-a6ad-41b4-b321-0510745f16cf46.MirrorCS"),sQuery(id+"F0.wireOp",EDGE,"dc92d004-a6ad-41b4-b321-0510745f16cf49.MirrorCS"),sQuery(id+"F0.wireOp",EDGE,"dc92d004-a6ad-41b4-b321-0510745f16cf52.MirrorC"),sQuery(id+"F0.wireOp",EDGE,"dc92d004-a6ad-41b4-b321-0510745f16cf53.MirrorCS"),sQuery(id+"F0.wireOp",EDGE,"dc92d004-a6ad-41b4-b321-0510745f16cf54.MirrorCS"),sQuery(id+"F0.wireOp",EDGE,"dc92d004-a6ad-41b4-b321-0510745f16cf55.MirrorCS"),sQuery(id+"F0.wireOp",EDGE,"E25"),sQuery(id+"F0.wireOp",EDGE,"E26"),sQuery(id+"F0.wireOp",EDGE,"ffa57ce4-e106-4af1-8c53-b98dc5f750d70.MirrorC"),sQuery(id+"F0.wireOp",EDGE,"3e98f3d7-1223-4975-97da-47207ce6f79a0.MirrorC")])],"isStart":true});
            var sketch = newSketch(context, id + "F4", { "sketchPlane" : qUnion([Q0])});
            skCircle(sketch, "E137", {"center": v(-157.56, 27.6) * mm, "radius": 5.9 * mm});
            skCircle(sketch, "E138", {"center": v(-157.56, -27.6) * mm, "radius": 5.9 * mm});
            skSolve(sketch);
        }
        {
            var Q0;
            Q0=qSketchRegion(id+"F4",true);
            extrude(context, id + "F5", {"entities" : qUnion([Q0]), "operationType" : NewBodyOperationType.REMOVE, "oppositeDirection" : true, "depth" : 1.5 * mm});
        }
    });
